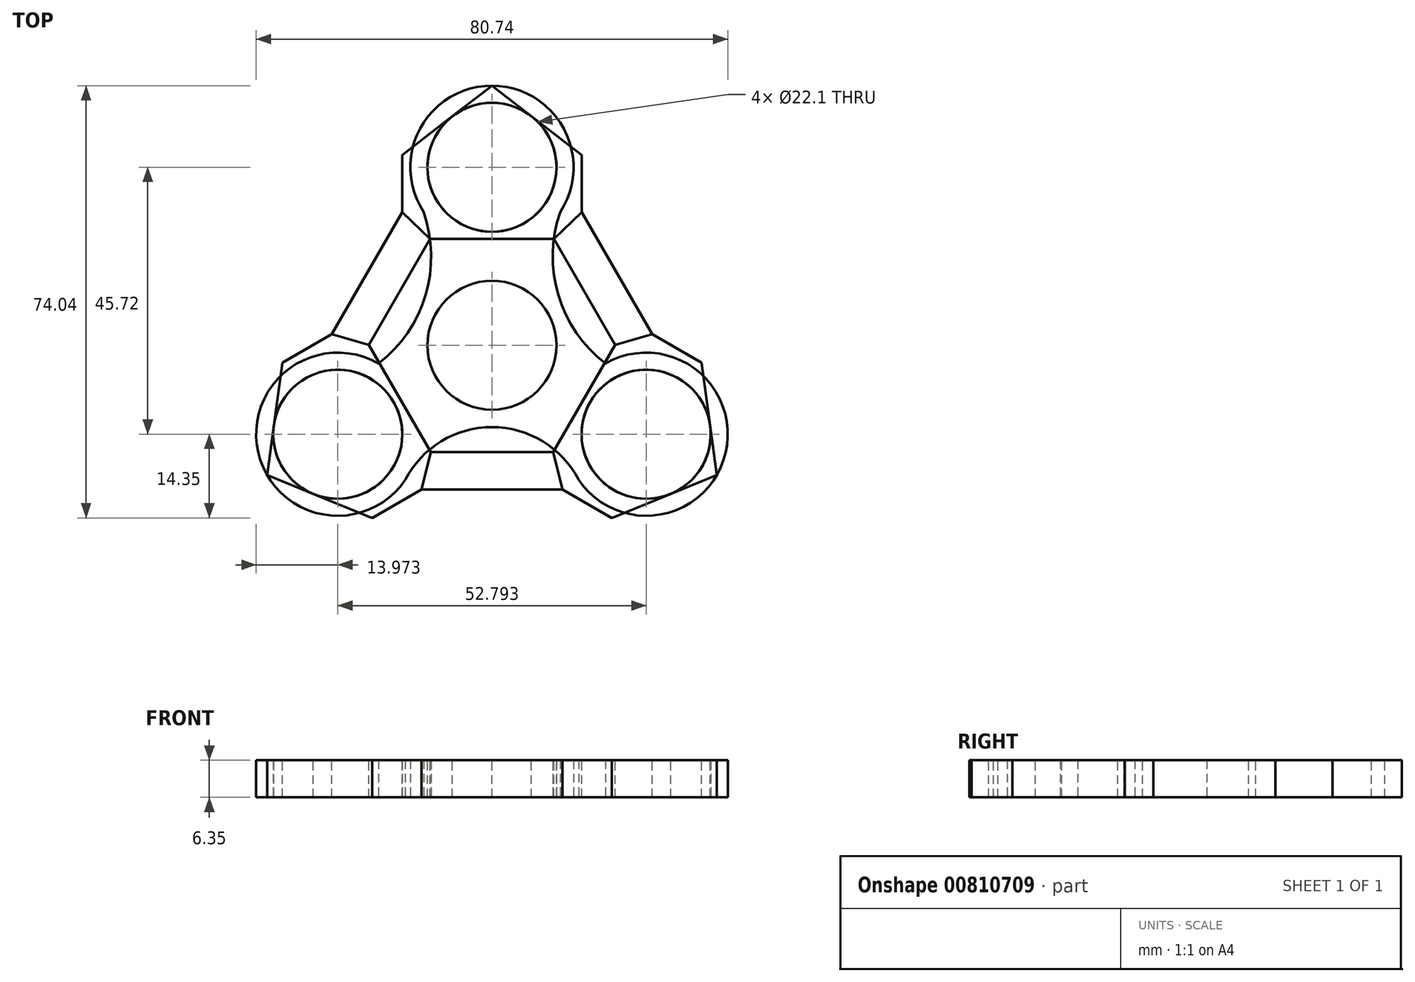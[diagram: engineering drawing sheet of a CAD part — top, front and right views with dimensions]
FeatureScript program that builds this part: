
annotation { "Feature Type Name" : "Feature", "Feature Type Description" : "" }
export const myFeature = defineFeature(function(context is Context, id is Id, definition is map)
    precondition{}
    {
        {
            var Q0;
            Q0=qCreatedBy(makeId("Top.planeOp"),FACE);
            var sketch = newSketch(context, id + "F0", { "sketchPlane" : qUnion([Q0])});
            skCircle(sketch, "E0", {"center": v(0, 0) * mm, "radius": 44.45 * mm});
            skCircle(sketch, "E1", {"center": v(0, 0) * mm, "radius": 11.05 * mm});
            skLineSegment(sketch, "E2", {"start": v(0, 0) * mm, "end": v(0, 30.48) * mm, "construction": true});
            skCircle(sketch, "E3", {"center": v(0, 30.48) * mm, "radius": 11.05 * mm});
            skCircle(sketch, "E4.1.0", {"center": v(-26.4, -15.24) * mm, "radius": 11.05 * mm});
            skCircle(sketch, "E4.2.0", {"center": v(26.4, -15.24) * mm, "radius": 11.05 * mm});
            skCircle(sketch, "E5", {"center": v(0, 0) * mm, "radius": 13.97 * mm});
            skCircle(sketch, "E6", {"center": v(0, 30.48) * mm, "radius": 13.97 * mm});
            skCircle(sketch, "E7", {"center": v(-26.4, -15.24) * mm, "radius": 13.97 * mm});
            skCircle(sketch, "E8", {"center": v(26.4, -15.24) * mm, "radius": 13.97 * mm});
            skArc(sketch, "E9", {"start": v(-19.41, -3.14) * mm, "mid": v(-11.38, 8.6) * mm, "end": v(-11.68, 22.81) * mm});
            skArc(sketch, "E10", {"start": v(11.68, 22.81) * mm, "mid": v(11.38, 8.6) * mm, "end": v(19.41, -3.14) * mm});
            skArc(sketch, "E11", {"start": v(14.84, -23.1) * mm, "mid": v(0, -14.02) * mm, "end": v(-14.84, -23.1) * mm});
            skSolve(sketch);
        }
        {
            var Q0;
            Q0=makeQuery(id+"F0.imprint","IMPRINT",FACE,{"disambiguationData":[TD([[makeQuery(id+"F0.imprint","IMPRINT",EDGE,{"derivedFrom":sQuery(id+"F0.wireOp",EDGE,"E3")}),-1.0]])]});
            var Q1;
            Q1=makeQuery(id+"F0.imprint","IMPRINT",FACE,{"disambiguationData":[TD([[makeQuery(id+"F0.imprint","IMPRINT",EDGE,{"derivedFrom":sQuery(id+"F0.wireOp",EDGE,"E4.2.0")}),-1.0]])]});
            var Q2;
            Q2=makeQuery(id+"F0.imprint","IMPRINT",FACE,{"disambiguationData":[TD([[makeQuery(id+"F0.imprint","IMPRINT",EDGE,{"derivedFrom":sQuery(id+"F0.wireOp",EDGE,"E4.1.0")}),-1.0]])]});
            var Q3;
            Q3=makeQuery(id+"F0.imprint","IMPRINT",FACE,{"disambiguationData":[TD([[makeQuery(id+"F0.imprint","IMPRINT",EDGE,{"derivedFrom":sQuery(id+"F0.wireOp",EDGE,"E1")}),-1.0]])]});
            var Q4;
            {var subQ0=sQuery(id+"F0.wireOp",EDGE,"E10");var subQ9=sQuery(id+"F0.wireOp",EDGE,"E5");var subQ11=makeQuery(id+"F0.imprint","INTERSECT",VERTEX,{"disambiguationData":[OD(1.0)],"derivedFrom":[subQ9,subQ0]});Q4=makeQuery(id+"F0.imprint","IMPRINT",FACE,{"disambiguationData":[TD([[makeQuery(id+"F0.imprint","IMPRINT",EDGE,{"disambiguationData":[TD([[subQ11,1.0]])],"derivedFrom":subQ9}),-1.0]])]});}
            var Q5;
            {var subQ0=sQuery(id+"F0.wireOp",EDGE,"E10");var subQ1=sQuery(id+"F0.wireOp",EDGE,"E5");var subQ2=makeQuery(id+"F0.imprint","INTERSECT",VERTEX,{"disambiguationData":[OD(0.0)],"derivedFrom":[subQ1,subQ0]});Q5=makeQuery(id+"F0.imprint","IMPRINT",FACE,{"disambiguationData":[TD([[makeQuery(id+"F0.imprint","IMPRINT",EDGE,{"disambiguationData":[TD([[subQ2,-1.0]])],"derivedFrom":subQ1}),-1.0]])]});}
            extrude(context, id + "F1", {"entities" : qUnion([Q0, Q1, Q2, Q3, Q4, Q5]), "depth" : 6.35 * mm, "offsetDistance" : 25.4 * mm});
        }
        {
            var Q0;
            Q0=makeQuery(id+"F1.opExtrude","CAP_FACE",FACE,{"disambiguationData":[OSD([sQuery(id+"F0.wireOp",EDGE,"E1"),sQuery(id+"F0.wireOp",EDGE,"E3"),sQuery(id+"F0.wireOp",EDGE,"E4.1.0"),sQuery(id+"F0.wireOp",EDGE,"E4.2.0"),sQuery(id+"F0.wireOp",EDGE,"E6"),sQuery(id+"F0.wireOp",EDGE,"E7"),sQuery(id+"F0.wireOp",EDGE,"E8"),sQuery(id+"F0.wireOp",EDGE,"E9"),sQuery(id+"F0.wireOp",EDGE,"E10"),sQuery(id+"F0.wireOp",EDGE,"E11")])],"isStart":false});
            var sketch = newSketch(context, id + "F2", { "sketchPlane" : qUnion([Q0])});
            skLineSegment(sketch, "E12", {"start": v(0, 44.45) * mm, "end": v(-15.37, 32.56) * mm});
            skLineSegment(sketch, "E13", {"start": v(-15.37, 32.56) * mm, "end": v(-15.37, 22.81) * mm});
            skLineSegment(sketch, "E14", {"start": v(-15.37, 22.81) * mm, "end": v(-10.6, 18.22) * mm});
            skLineSegment(sketch, "E15", {"start": v(-10.6, 18.22) * mm, "end": v(10.6, 18.22) * mm});
            skLineSegment(sketch, "E16", {"start": v(0, 44.45) * mm, "end": v(15.37, 32.56) * mm});
            skLineSegment(sketch, "E17", {"start": v(-15.37, 22.81) * mm, "end": v(19.41, 22.81) * mm, "construction": true});
            skLineSegment(sketch, "E18", {"start": v(15.37, 32.56) * mm, "end": v(15.37, 22.8) * mm});
            skLineSegment(sketch, "E19", {"start": v(15.37, 22.8) * mm, "end": v(10.6, 18.22) * mm});
            skLineSegment(sketch, "E20.1.0", {"start": v(-38.5, -22.22) * mm, "end": v(-20.51, -29.59) * mm});
            skLineSegment(sketch, "E20.1.1", {"start": v(-38.5, -22.22) * mm, "end": v(-35.88, -2.97) * mm});
            skLineSegment(sketch, "E20.1.2", {"start": v(-35.88, -2.97) * mm, "end": v(-27.43, 1.9) * mm});
            skLineSegment(sketch, "E20.1.3", {"start": v(-27.43, 1.9) * mm, "end": v(-21.08, 0.07) * mm});
            skLineSegment(sketch, "E20.1.4", {"start": v(-10.48, -18.3) * mm, "end": v(-21.08, 0.07) * mm});
            skLineSegment(sketch, "E20.1.5", {"start": v(-12.07, -24.72) * mm, "end": v(-10.48, -18.3) * mm});
            skLineSegment(sketch, "E20.1.6", {"start": v(-20.51, -29.59) * mm, "end": v(-12.07, -24.72) * mm});
            skLineSegment(sketch, "E20.2.0", {"start": v(38.5, -22.23) * mm, "end": v(35.88, -2.97) * mm});
            skLineSegment(sketch, "E20.2.1", {"start": v(38.5, -22.23) * mm, "end": v(20.51, -29.59) * mm});
            skLineSegment(sketch, "E20.2.2", {"start": v(20.51, -29.59) * mm, "end": v(12.06, -24.71) * mm});
            skLineSegment(sketch, "E20.2.3", {"start": v(12.06, -24.71) * mm, "end": v(10.48, -18.3) * mm});
            skLineSegment(sketch, "E20.2.4", {"start": v(21.08, 0.07) * mm, "end": v(10.48, -18.3) * mm});
            skLineSegment(sketch, "E20.2.5", {"start": v(27.44, 1.9) * mm, "end": v(21.08, 0.07) * mm});
            skLineSegment(sketch, "E20.2.6", {"start": v(35.88, -2.97) * mm, "end": v(27.44, 1.9) * mm});
            skPoint(sketch, "E20.center", {"position": v(0, 0) * mm});
            skLineSegment(sketch, "E21", {"start": v(-15.37, 22.81) * mm, "end": v(-27.43, 1.9) * mm});
            skLineSegment(sketch, "E22", {"start": v(-21.08, 0.07) * mm, "end": v(-10.6, 18.22) * mm});
            skLineSegment(sketch, "E23", {"start": v(10.6, 18.22) * mm, "end": v(21.08, 0.07) * mm});
            skLineSegment(sketch, "E24", {"start": v(15.37, 22.8) * mm, "end": v(27.44, 1.9) * mm});
            skLineSegment(sketch, "E25", {"start": v(-10.48, -18.3) * mm, "end": v(10.48, -18.3) * mm});
            skLineSegment(sketch, "E26", {"start": v(-12.07, -24.72) * mm, "end": v(12.06, -24.71) * mm});
            skSolve(sketch);
        }
        {
            var Q0;
            {var subQ1=sQuery(id+"F2.wireOp",EDGE,"E12");var subQ3=makeQuery(id+"F1.opExtrude","CAP_EDGE",EDGE,{"disambiguationData":[OSD([sQuery(id+"F0.wireOp",EDGE,"E3")])],"isStart":false});var subQ4=makeQuery(id+"F2.imprint","INTERSECT",VERTEX,{"derivedFrom":[subQ3,subQ1]});Q0=makeQuery(id+"F2.imprint","IMPRINT",FACE,{"disambiguationData":[TD([[makeQuery(id+"F2.imprint","IMPRINT",EDGE,{"disambiguationData":[TD([[subQ4,1.0]])],"derivedFrom":subQ3}),-1.0]])]});}
            var Q1;
            {var subQ1=sQuery(id+"F2.wireOp",EDGE,"E20.1.0");var subQ3=makeQuery(id+"F1.opExtrude","CAP_EDGE",EDGE,{"disambiguationData":[OSD([sQuery(id+"F0.wireOp",EDGE,"E4.1.0")])],"isStart":false});var subQ4=makeQuery(id+"F2.imprint","INTERSECT",VERTEX,{"derivedFrom":[subQ3,subQ1]});Q1=makeQuery(id+"F2.imprint","IMPRINT",FACE,{"disambiguationData":[TD([[makeQuery(id+"F2.imprint","IMPRINT",EDGE,{"disambiguationData":[TD([[subQ4,1.0]])],"derivedFrom":subQ3}),-1.0]])]});}
            var Q2;
            {var subQ1=sQuery(id+"F2.wireOp",EDGE,"E20.2.0");var subQ3=makeQuery(id+"F1.opExtrude","CAP_EDGE",EDGE,{"disambiguationData":[OSD([sQuery(id+"F0.wireOp",EDGE,"E4.2.0")])],"isStart":false});var subQ4=makeQuery(id+"F2.imprint","INTERSECT",VERTEX,{"derivedFrom":[subQ3,subQ1]});Q2=makeQuery(id+"F2.imprint","IMPRINT",FACE,{"disambiguationData":[TD([[makeQuery(id+"F2.imprint","IMPRINT",EDGE,{"disambiguationData":[TD([[subQ4,1.0]])],"derivedFrom":subQ3}),-1.0]])]});}
            var Q3;
            {var subQ6=sQuery(id+"F2.wireOp",EDGE,"E13");Q3=makeQuery(id+"F2.imprint","IMPRINT",FACE,{"disambiguationData":[TD([[makeQuery(id+"F2.imprint","IMPRINT",EDGE,{"derivedFrom":subQ6}),1.0]])]});}
            var Q4;
            {var subQ6=sQuery(id+"F2.wireOp",EDGE,"E18");Q4=makeQuery(id+"F2.imprint","IMPRINT",FACE,{"disambiguationData":[TD([[makeQuery(id+"F2.imprint","IMPRINT",EDGE,{"derivedFrom":subQ6}),-1.0]])]});}
            var Q5;
            {var subQ0=sQuery(id+"F2.wireOp",EDGE,"E20.1.5");Q5=makeQuery(id+"F2.imprint","IMPRINT",FACE,{"disambiguationData":[TD([[makeQuery(id+"F2.imprint","IMPRINT",EDGE,{"derivedFrom":subQ0}),1.0]])]});}
            var Q6;
            {var subQ6=sQuery(id+"F2.wireOp",EDGE,"E20.1.2");Q6=makeQuery(id+"F2.imprint","IMPRINT",FACE,{"disambiguationData":[TD([[makeQuery(id+"F2.imprint","IMPRINT",EDGE,{"derivedFrom":subQ6}),-1.0]])]});}
            var Q7;
            {var subQ0=sQuery(id+"F2.wireOp",EDGE,"E20.2.5");Q7=makeQuery(id+"F2.imprint","IMPRINT",FACE,{"disambiguationData":[TD([[makeQuery(id+"F2.imprint","IMPRINT",EDGE,{"derivedFrom":subQ0}),1.0]])]});}
            var Q8;
            {var subQ1=sQuery(id+"F2.wireOp",EDGE,"E20.2.2");Q8=makeQuery(id+"F2.imprint","IMPRINT",FACE,{"disambiguationData":[TD([[makeQuery(id+"F2.imprint","IMPRINT",EDGE,{"derivedFrom":subQ1}),-1.0]])]});}
            var Q9;
            {var subQ5=sQuery(id+"F2.wireOp",EDGE,"E15");Q9=makeQuery(id+"F2.imprint","IMPRINT",FACE,{"disambiguationData":[TD([[makeQuery(id+"F2.imprint","IMPRINT",EDGE,{"derivedFrom":subQ5}),1.0]])]});}
            var Q10;
            {var subQ1=makeQuery(id+"F1.opExtrude","CAP_EDGE",EDGE,{"disambiguationData":[OSD([sQuery(id+"F0.wireOp",EDGE,"E7")])],"isStart":false});var subQ12=sQuery(id+"F2.wireOp",EDGE,"E20.1.0");var subQ13=makeQuery(id+"F2.imprint","INTERSECT",VERTEX,{"derivedFrom":[subQ1,subQ12]});Q10=makeQuery(id+"F2.imprint","IMPRINT",FACE,{"disambiguationData":[TD([[makeQuery(id+"F2.imprint","IMPRINT",EDGE,{"disambiguationData":[TD([[subQ13,1.0]])],"derivedFrom":subQ12}),1.0]])]});}
            var Q11;
            {var subQ1=makeQuery(id+"F1.opExtrude","CAP_EDGE",EDGE,{"disambiguationData":[OSD([sQuery(id+"F0.wireOp",EDGE,"E8")])],"isStart":false});var subQ3=sQuery(id+"F2.wireOp",EDGE,"E20.2.0");var subQ4=makeQuery(id+"F2.imprint","INTERSECT",VERTEX,{"derivedFrom":[subQ1,subQ3]});Q11=makeQuery(id+"F2.imprint","IMPRINT",FACE,{"disambiguationData":[TD([[makeQuery(id+"F2.imprint","IMPRINT",EDGE,{"disambiguationData":[TD([[subQ4,1.0]])],"derivedFrom":subQ3}),1.0]])]});}
            extrude(context, id + "F3", {"entities" : qUnion([Q0, Q1, Q2, Q3, Q4, Q5, Q6, Q7, Q8, Q9, Q10, Q11]), "oppositeDirection" : true, "depth" : 6.35 * mm, "offsetDistance" : 25.4 * mm});
        }
        {
            var Q0;
            Q0=makeQuery(id+"F2.imprint","IMPRINT",FACE,{"disambiguationData":[TD([[makeQuery(id+"F2.imprint","IMPRINT",EDGE,{"derivedFrom":sQuery(id+"F2.wireOp",EDGE,"E14")}),-1.0]])]});
            var Q1;
            Q1=makeQuery(id+"F2.imprint","IMPRINT",FACE,{"disambiguationData":[TD([[makeQuery(id+"F2.imprint","IMPRINT",EDGE,{"derivedFrom":sQuery(id+"F2.wireOp",EDGE,"E19")}),1.0]])]});
            var Q2;
            Q2=makeQuery(id+"F2.imprint","IMPRINT",FACE,{"disambiguationData":[TD([[makeQuery(id+"F2.imprint","IMPRINT",EDGE,{"derivedFrom":sQuery(id+"F2.wireOp",EDGE,"E20.1.5")}),-1.0]])]});
            var Q3;
            Q3=sQuery(id+"F2.wireOp",EDGE,"E21");
            var Q4;
            Q4=sQuery(id+"F2.wireOp",EDGE,"E22");
            extrude(context, id + "F4", {"entities" : qUnion([Q0, Q1, Q2]), "surfaceEntities" : qUnion([Q3, Q4]), "oppositeDirection" : true, "depth" : 6.35 * mm, "offsetDistance" : 25.4 * mm});
        }
    });
